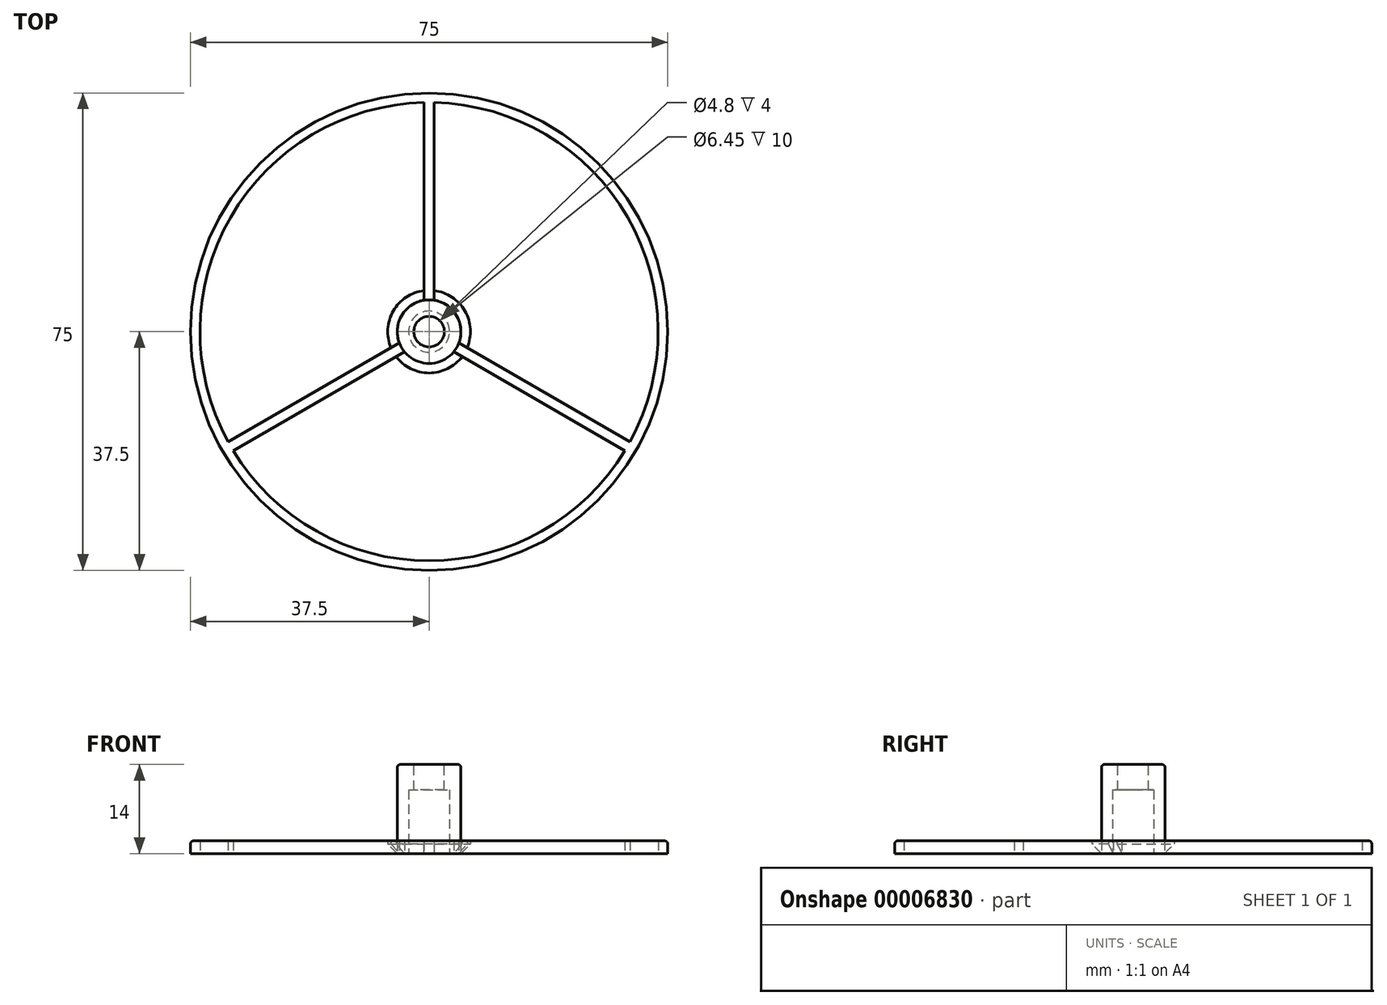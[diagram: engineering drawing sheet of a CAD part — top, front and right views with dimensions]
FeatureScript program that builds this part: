
annotation { "Feature Type Name" : "Feature", "Feature Type Description" : "" }
export const myFeature = defineFeature(function(context is Context, id is Id, definition is map)
    precondition{}
    {
        {
            var Q0;
            Q0=qCreatedBy(makeId("Top.planeOp"),FACE);
            var sketch = newSketch(context, id + "F0", { "sketchPlane" : qUnion([Q0])});
            skCircle(sketch, "E0", {"center": v(0, 0) * mm, "radius": 5 * mm});
            skCircle(sketch, "E1", {"center": v(0, 0) * mm, "radius": 36 * mm});
            skLineSegment(sketch, "E2", {"start": v(-0.8, 4.94) * mm, "end": v(-0.8, 36) * mm});
            skLineSegment(sketch, "E3.0.MirrorCS", {"start": v(0.8, 4.94) * mm, "end": v(0.8, 36) * mm});
            skLineSegment(sketch, "E4.1.0", {"start": v(-4.67, -1.78) * mm, "end": v(-31.57, -17.3) * mm});
            skLineSegment(sketch, "E4.1.1", {"start": v(-3.87, -3.16) * mm, "end": v(-30.77, -18.69) * mm});
            skLineSegment(sketch, "E4.2.0", {"start": v(3.87, -3.16) * mm, "end": v(30.77, -18.69) * mm});
            skLineSegment(sketch, "E4.2.1", {"start": v(4.67, -1.78) * mm, "end": v(31.57, -17.3) * mm});
            skCircle(sketch, "E5", {"center": v(0, 0) * mm, "radius": 37.5 * mm});
            skSolve(sketch);
        }
        {
            var Q0;
            Q0=makeQuery(id+"F0.imprint","IMPRINT",FACE,{"disambiguationData":[TD([[makeQuery(id+"F0.imprint","IMPRINT",EDGE,{"derivedFrom":sQuery(id+"F0.wireOp",EDGE,"E5")}),1.0]])]});
            var Q1;
            {var subQ1=sQuery(id+"F0.wireOp",EDGE,"E2");Q1=makeQuery(id+"F0.imprint","IMPRINT",FACE,{"disambiguationData":[TD([[makeQuery(id+"F0.imprint","IMPRINT",EDGE,{"derivedFrom":subQ1}),-1.0]])]});}
            var Q2;
            {var subQ0=sQuery(id+"F0.wireOp",EDGE,"E4.2.0");Q2=makeQuery(id+"F0.imprint","IMPRINT",FACE,{"disambiguationData":[TD([[makeQuery(id+"F0.imprint","IMPRINT",EDGE,{"derivedFrom":subQ0}),1.0]])]});}
            var Q3;
            {var subQ0=sQuery(id+"F0.wireOp",EDGE,"E4.1.0");Q3=makeQuery(id+"F0.imprint","IMPRINT",FACE,{"disambiguationData":[TD([[makeQuery(id+"F0.imprint","IMPRINT",EDGE,{"derivedFrom":subQ0}),1.0]])]});}
            var Q4;
            {var subQ0=sQuery(id+"F0.wireOp",EDGE,"E0");var subQ6=makeQuery(id+"F0.imprint","INTERSECT",VERTEX,{"derivedFrom":[subQ0,sQuery(id+"F0.wireOp",EDGE,"E2")]});Q4=makeQuery(id+"F0.imprint","IMPRINT",FACE,{"disambiguationData":[TD([[makeQuery(id+"F0.imprint","IMPRINT",EDGE,{"disambiguationData":[TD([[subQ6,1.0]])],"derivedFrom":subQ0}),1.0]])]});}
            extrude(context, id + "F1", {"entities" : qUnion([Q0, Q1, Q2, Q3, Q4]), "depth" : 2 * mm});
        }
        {
            var Q0;
            Q0=makeQuery(id+"F1.opExtrude","CAP_FACE",FACE,{"disambiguationData":[OSD([sQuery(id+"F0.wireOp",EDGE,"E0"),sQuery(id+"F0.wireOp",EDGE,"E1"),sQuery(id+"F0.wireOp",EDGE,"E2"),sQuery(id+"F0.wireOp",EDGE,"E3.0.MirrorCS"),sQuery(id+"F0.wireOp",EDGE,"E4.1.0"),sQuery(id+"F0.wireOp",EDGE,"E4.1.1"),sQuery(id+"F0.wireOp",EDGE,"E4.2.0"),sQuery(id+"F0.wireOp",EDGE,"E4.2.1"),sQuery(id+"F0.wireOp",EDGE,"E5")])],"isStart":false});
            var sketch = newSketch(context, id + "F2", { "sketchPlane" : qUnion([Q0])});
            skCircle(sketch, "E6", {"center": v(0, 0) * mm, "radius": 5 * mm});
            skSolve(sketch);
        }
        {
            var Q0;
            Q0=qSketchRegion(id+"F2",true);
            extrude(context, id + "F3", {"entities" : qUnion([Q0]), "operationType" : NewBodyOperationType.ADD, "depth" : 12 * mm});
        }
        {
            var Q0;
            Q0=makeQuery(id+"F3.opExtrude","CAP_FACE",FACE,{"disambiguationData":[OSD([sQuery(id+"F2.wireOp",EDGE,"E6")])],"isStart":false});
            var sketch = newSketch(context, id + "F4", { "sketchPlane" : qUnion([Q0])});
            skCircle(sketch, "E7", {"center": v(0, 0) * mm, "radius": 2.4 * mm});
            skSolve(sketch);
        }
        {
            var Q0;
            Q0=qSketchRegion(id+"F4",true);
            extrude(context, id + "F5", {"entities" : qUnion([Q0]), "operationType" : NewBodyOperationType.REMOVE, "oppositeDirection" : true, "depth" : 4 * mm});
        }
        {
            var Q0;
            Q0=makeQuery(id+"F3.opExtrude","CAP_EDGE",EDGE,{"disambiguationData":[OSD([sQuery(id+"F2.wireOp",EDGE,"E6")])],"isStart":false});
            var Q1;
            Q1=makeQuery(id+"F1.opExtrude","CAP_EDGE",EDGE,{"disambiguationData":[OSD([sQuery(id+"F0.wireOp",EDGE,"E5")])],"isStart":false});
            fillet(context, id + "F6", {"entities" : qUnion([Q0, Q1]), "radius" : .5 * mm, "tangentPropagation" : true, "allowEdgeOverflow" : false});
        }
        {
            var Q0;
            Q0=makeQuery(id+"F1.opExtrude","CAP_FACE",FACE,{"disambiguationData":[OSD([sQuery(id+"F0.wireOp",EDGE,"E0"),sQuery(id+"F0.wireOp",EDGE,"E1"),sQuery(id+"F0.wireOp",EDGE,"E2"),sQuery(id+"F0.wireOp",EDGE,"E3.0.MirrorCS"),sQuery(id+"F0.wireOp",EDGE,"E4.1.0"),sQuery(id+"F0.wireOp",EDGE,"E4.1.1"),sQuery(id+"F0.wireOp",EDGE,"E4.2.0"),sQuery(id+"F0.wireOp",EDGE,"E4.2.1"),sQuery(id+"F0.wireOp",EDGE,"E5")])],"isStart":true});
            var sketch = newSketch(context, id + "F7", { "sketchPlane" : qUnion([Q0])});
            skCircle(sketch, "E8", {"center": v(0, 0) * mm, "radius": 3.23 * mm});
            skSolve(sketch);
        }
        {
            var Q0;
            Q0=makeQuery(id+"F7.imprint","IMPRINT",FACE,{"disambiguationData":[TD([[makeQuery(id+"F7.imprint","IMPRINT",EDGE,{"derivedFrom":sQuery(id+"F7.wireOp",EDGE,"E8")}),1.0]])]});
            extrude(context, id + "F8", {"entities" : qUnion([Q0]), "operationType" : NewBodyOperationType.REMOVE, "oppositeDirection" : true, "depth" : 10 * mm});
        }
        {
            var Q0;
            Q0=makeQuery(id+"F1.opExtrude","CAP_FACE",FACE,{"disambiguationData":[OSD([sQuery(id+"F0.wireOp",EDGE,"E0"),sQuery(id+"F0.wireOp",EDGE,"E1"),sQuery(id+"F0.wireOp",EDGE,"E2"),sQuery(id+"F0.wireOp",EDGE,"E3.0.MirrorCS"),sQuery(id+"F0.wireOp",EDGE,"E4.1.0"),sQuery(id+"F0.wireOp",EDGE,"E4.1.1"),sQuery(id+"F0.wireOp",EDGE,"E4.2.0"),sQuery(id+"F0.wireOp",EDGE,"E4.2.1"),sQuery(id+"F0.wireOp",EDGE,"E5")])],"isStart":true});
            var sketch = newSketch(context, id + "F9", { "sketchPlane" : qUnion([Q0])});
            skCircle(sketch, "E9", {"center": v(0, 0) * mm, "radius": 6.5 * mm});
            skSolve(sketch);
        }
        {
            var Q0;
            {var subQ4=sQuery(id+"F0.wireOp",EDGE,"E0");var subQ5=sQuery(id+"F0.wireOp",EDGE,"E4.1.1");var subQ6=makeQuery(id+"F1.opExtrude","CAP_EDGE",EDGE,{"disambiguationData":[OSD([subQ4]),TDD([makeQuery(id+"F0.imprint","IMPRINT",EDGE,{"disambiguationData":[TD([[makeQuery(id+"F0.imprint","INTERSECT",VERTEX,{"derivedFrom":[subQ4,subQ5]}),-1.0]])],"derivedFrom":subQ4})])],"isStart":true});Q0=makeQuery(id+"F9.imprint","IMPRINT",FACE,{"disambiguationData":[TD([[makeQuery(id+"F9.imprint","IMPRINT",EDGE,{"derivedFrom":subQ6}),1.0]])]});}
            var Q1;
            {var subQ4=sQuery(id+"F0.wireOp",EDGE,"E0");var subQ5=sQuery(id+"F0.wireOp",EDGE,"E2");var subQ6=makeQuery(id+"F1.opExtrude","CAP_EDGE",EDGE,{"disambiguationData":[OSD([subQ4]),TDD([makeQuery(id+"F0.imprint","IMPRINT",EDGE,{"disambiguationData":[TD([[makeQuery(id+"F0.imprint","INTERSECT",VERTEX,{"derivedFrom":[subQ4,subQ5]}),-1.0]])],"derivedFrom":subQ4})])],"isStart":true});Q1=makeQuery(id+"F9.imprint","IMPRINT",FACE,{"disambiguationData":[TD([[makeQuery(id+"F9.imprint","IMPRINT",EDGE,{"derivedFrom":subQ6}),1.0]])]});}
            var Q2;
            {var subQ4=sQuery(id+"F0.wireOp",EDGE,"E0");var subQ5=sQuery(id+"F0.wireOp",EDGE,"E3.0.MirrorCS");var subQ6=makeQuery(id+"F1.opExtrude","CAP_EDGE",EDGE,{"disambiguationData":[OSD([subQ4]),TDD([makeQuery(id+"F0.imprint","IMPRINT",EDGE,{"disambiguationData":[TD([[makeQuery(id+"F0.imprint","INTERSECT",VERTEX,{"derivedFrom":[subQ4,subQ5]}),1.0]])],"derivedFrom":subQ4})])],"isStart":true});Q2=makeQuery(id+"F9.imprint","IMPRINT",FACE,{"disambiguationData":[TD([[makeQuery(id+"F9.imprint","IMPRINT",EDGE,{"derivedFrom":subQ6}),1.0]])]});}
            extrude(context, id + "F10", {"entities" : qUnion([Q0, Q1, Q2]), "oppositeDirection" : true, "depth" : 2 * mm});
        }
        {
            var Q0;
            {var subQ0=sQuery(id+"F9.wireOp",EDGE,"E9");Q0=makeQuery(id+"F10.opExtrude","CAP_EDGE",EDGE,{"disambiguationData":[OSD([subQ0]),TDD([makeQuery(id+"F9.imprint","IMPRINT",EDGE,{"disambiguationData":[TD([[makeQuery(id+"F9.imprint","INTERSECT",VERTEX,{"derivedFrom":[makeQuery(id+"F1.opExtrude","CAP_EDGE",EDGE,{"disambiguationData":[OSD([sQuery(id+"F0.wireOp",EDGE,"E4.2.1")])],"isStart":true}),subQ0]}),1.0]])],"derivedFrom":subQ0})])],"isStart":true});}
            var Q1;
            {var subQ0=sQuery(id+"F9.wireOp",EDGE,"E9");Q1=makeQuery(id+"F10.opExtrude","CAP_EDGE",EDGE,{"disambiguationData":[OSD([subQ0]),TDD([makeQuery(id+"F9.imprint","IMPRINT",EDGE,{"disambiguationData":[TD([[makeQuery(id+"F9.imprint","INTERSECT",VERTEX,{"derivedFrom":[makeQuery(id+"F1.opExtrude","CAP_EDGE",EDGE,{"disambiguationData":[OSD([sQuery(id+"F0.wireOp",EDGE,"E4.2.0")])],"isStart":true}),subQ0]}),-1.0]])],"derivedFrom":subQ0})])],"isStart":true});}
            var Q2;
            {var subQ0=sQuery(id+"F9.wireOp",EDGE,"E9");Q2=makeQuery(id+"F10.opExtrude","CAP_EDGE",EDGE,{"disambiguationData":[OSD([subQ0]),TDD([makeQuery(id+"F9.imprint","IMPRINT",EDGE,{"disambiguationData":[TD([[makeQuery(id+"F9.imprint","INTERSECT",VERTEX,{"derivedFrom":[makeQuery(id+"F1.opExtrude","CAP_EDGE",EDGE,{"disambiguationData":[OSD([sQuery(id+"F0.wireOp",EDGE,"E4.1.0")])],"isStart":true}),subQ0]}),-1.0]])],"derivedFrom":subQ0})])],"isStart":true});}
            chamfer(context, id + "F11", {"entities" : qUnion([Q0, Q1, Q2]), "width" : 1.5 * mm, "tangentPropagation" : true});
        }
    });
